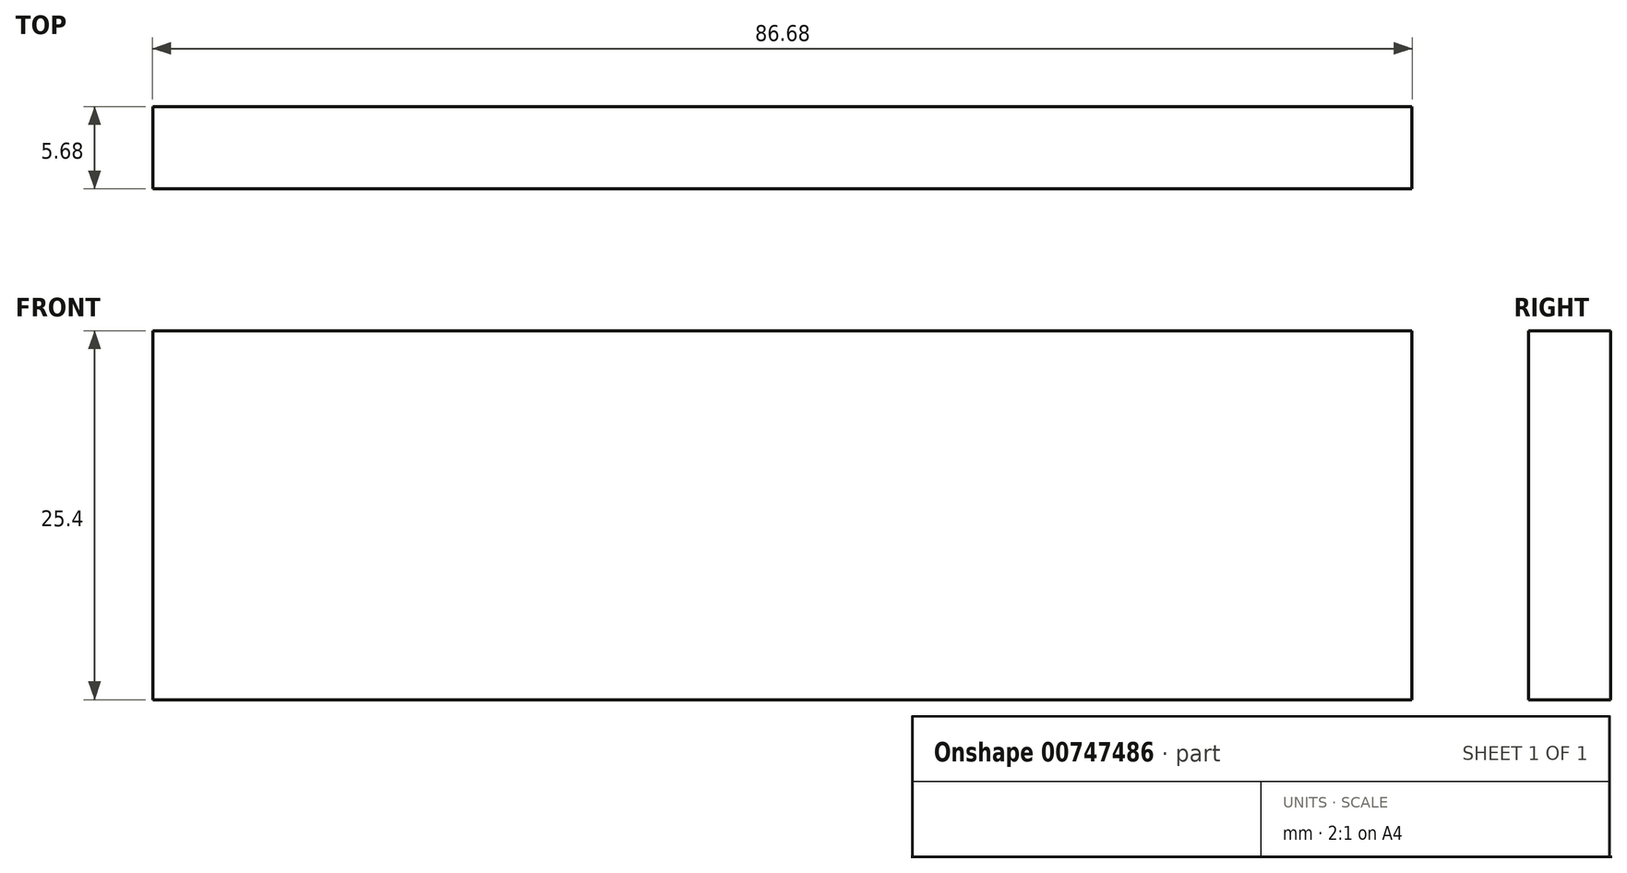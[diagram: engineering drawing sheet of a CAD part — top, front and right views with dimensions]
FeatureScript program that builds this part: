
annotation { "Feature Type Name" : "Feature", "Feature Type Description" : "" }
export const myFeature = defineFeature(function(context is Context, id is Id, definition is map)
    precondition{}
    {
        {
            var Q0;
            Q0=qCreatedBy(makeId("Top.planeOp"),FACE);
            var sketch = newSketch(context, id + "F0", { "sketchPlane" : qUnion([Q0])});
            skLineSegment(sketch, "E0.bottom", {"start": v(-39.22, 5.68) * mm, "end": v(47.46, 5.68) * mm});
            skLineSegment(sketch, "E0.top", {"start": v(-39.22, 0) * mm, "end": v(47.46, 0) * mm});
            skLineSegment(sketch, "E0.left", {"start": v(-39.22, 5.68) * mm, "end": v(-39.22, 0) * mm});
            skLineSegment(sketch, "E0.right", {"start": v(47.46, 5.68) * mm, "end": v(47.46, 0) * mm});
            skSolve(sketch);
        }
        {
            var Q0;
            Q0=makeQuery(id+"F0.imprint","IMPRINT",FACE,{"disambiguationData":[TD([[makeQuery(id+"F0.imprint","IMPRINT",EDGE,{"derivedFrom":sQuery(id+"F0.wireOp",EDGE,"E0.bottom")}),-1.0]])]});
            extrude(context, id + "F1", {"entities" : qUnion([Q0]), "depth" : 25.4 * mm, "offsetDistance" : 25.4 * mm});
        }
    });
